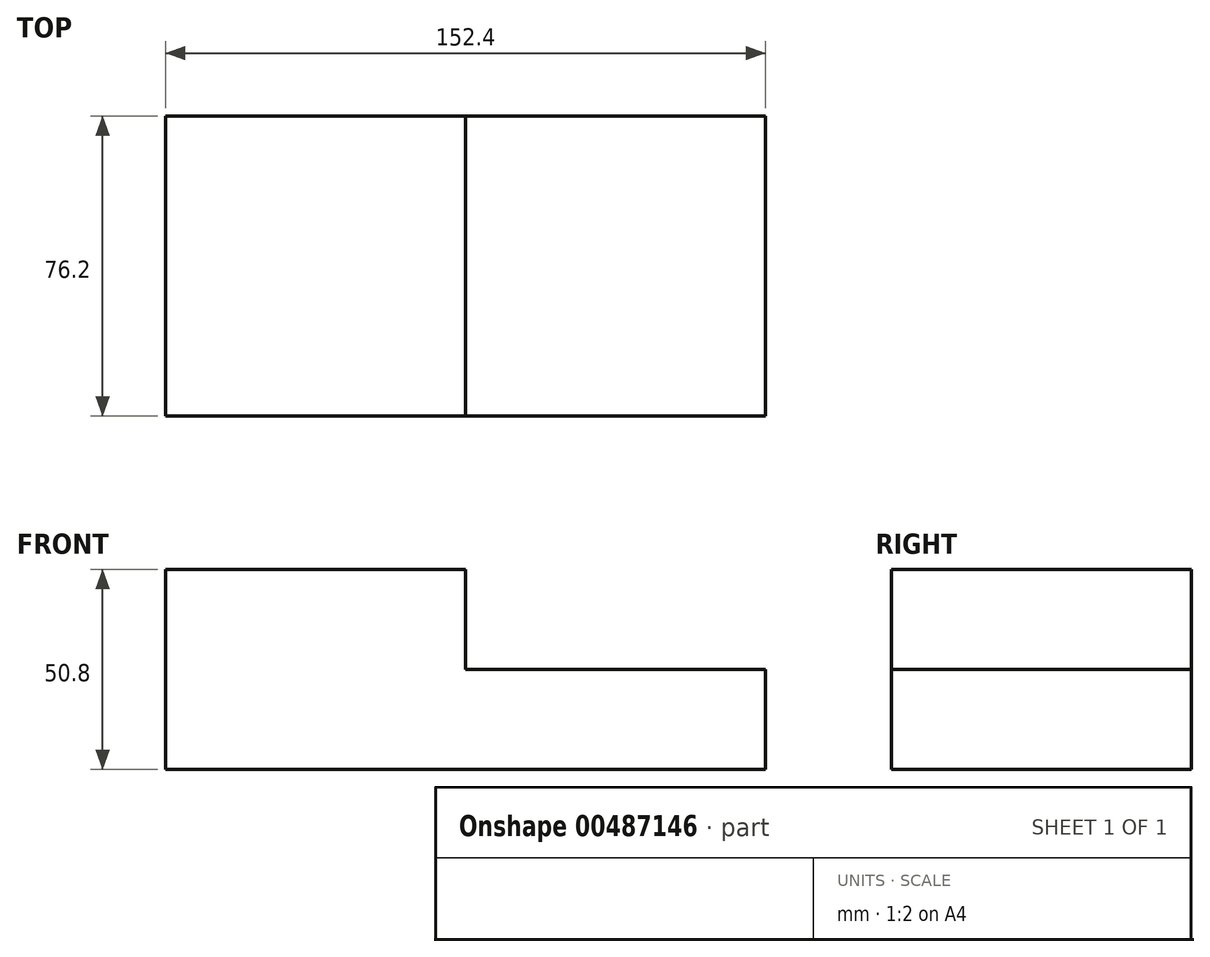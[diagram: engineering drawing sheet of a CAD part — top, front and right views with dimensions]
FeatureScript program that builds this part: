
annotation { "Feature Type Name" : "Feature", "Feature Type Description" : "" }
export const myFeature = defineFeature(function(context is Context, id is Id, definition is map)
    precondition{}
    {
        {
            var Q0;
            Q0=qCreatedBy(makeId("Front.planeOp"),FACE);
            var sketch = newSketch(context, id + "F0", { "sketchPlane" : qUnion([Q0])});
            skLineSegment(sketch, "E0", {"start": v(-130.83, 61) * mm, "end": v(-54.63, 61) * mm});
            skLineSegment(sketch, "E1", {"start": v(-54.63, 61) * mm, "end": v(-54.63, 35.6) * mm});
            skLineSegment(sketch, "E2", {"start": v(-54.63, 35.6) * mm, "end": v(21.57, 35.6) * mm});
            skLineSegment(sketch, "E3", {"start": v(-130.83, 61) * mm, "end": v(-130.83, 10.2) * mm});
            skLineSegment(sketch, "E4", {"start": v(-130.83, 10.2) * mm, "end": v(21.57, 10.2) * mm});
            skLineSegment(sketch, "E5", {"start": v(21.57, 35.6) * mm, "end": v(21.57, 10.2) * mm});
            skSolve(sketch);
        }
        {
            var Q0;
            Q0=makeQuery(id+"F0.imprint","IMPRINT",FACE,{"disambiguationData":[TD([[makeQuery(id+"F0.imprint","IMPRINT",EDGE,{"derivedFrom":sQuery(id+"F0.wireOp",EDGE,"E0")}),-1.0]])]});
            extrude(context, id + "F1", {"entities" : qUnion([Q0]), "depth" : 76.2 * mm});
        }
    });
